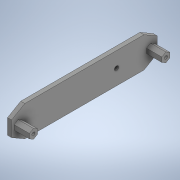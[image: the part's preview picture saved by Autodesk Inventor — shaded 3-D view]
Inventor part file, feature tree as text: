
AUTODESK INVENTOR PART (.ipt)
format: ipt  version: 2020 (Build 240168000, 168)  size: 260,096 bytes
history: native  units: in
note: dims shown in document units (in); Inventor stores cm internally (conversion verified against a paired STEP export)
features: extrude x6, sketch x6, plane x1
ambient origin geometry x8: Origin, YZ Plane, XZ Plane, XY Plane, X Axis, Y Axis, Z Axis, Center Point
bodies: Solid1 (feature_tree)
feature tree (13):
  extrude  "Extrusion1"  Depth=5.6299in
  extrude  "Extrusion3"  TaperAngle=0.0deg  [1 undecoded]
  extrude  "Extrusion4"  Depth=0.5906in
  plane  "Work Plane1"
  extrude  "Extrusion5"  Depth=0.122in
  extrude  "Extrusion6"  Depth=0.2402in
  extrude  "Extrusion7"  [1 undecoded]
  sketch  "Sketch1"  dims[d0=1.1811in d1=5.6299in]
  sketch  "Sketch2"  dims[d2=0.1575in d3=0.0in]
  sketch  "Sketch3"  dims[d8=0.315in d9=0.5906in]
  sketch  "Sketch4"  dims[d10=0.0in d12=0.122in]
  sketch  "Sketch5"  dims[d13=0.0in d14=0.0in d15=0.2402in]
  sketch  "Sketch8"  dims[d16=0.0866in d17=-0.2233in d18=-0.3937in d19=0.0866in d20=0.0in d26=1.5748in d27=0.1654in d30=0.0in d31=0.0in]
note: 2 required parameter values undecoded (feature->parameter linkage not recoverable at this tier; creation-order binding heuristic only, values carry confidence <= 0.55)
